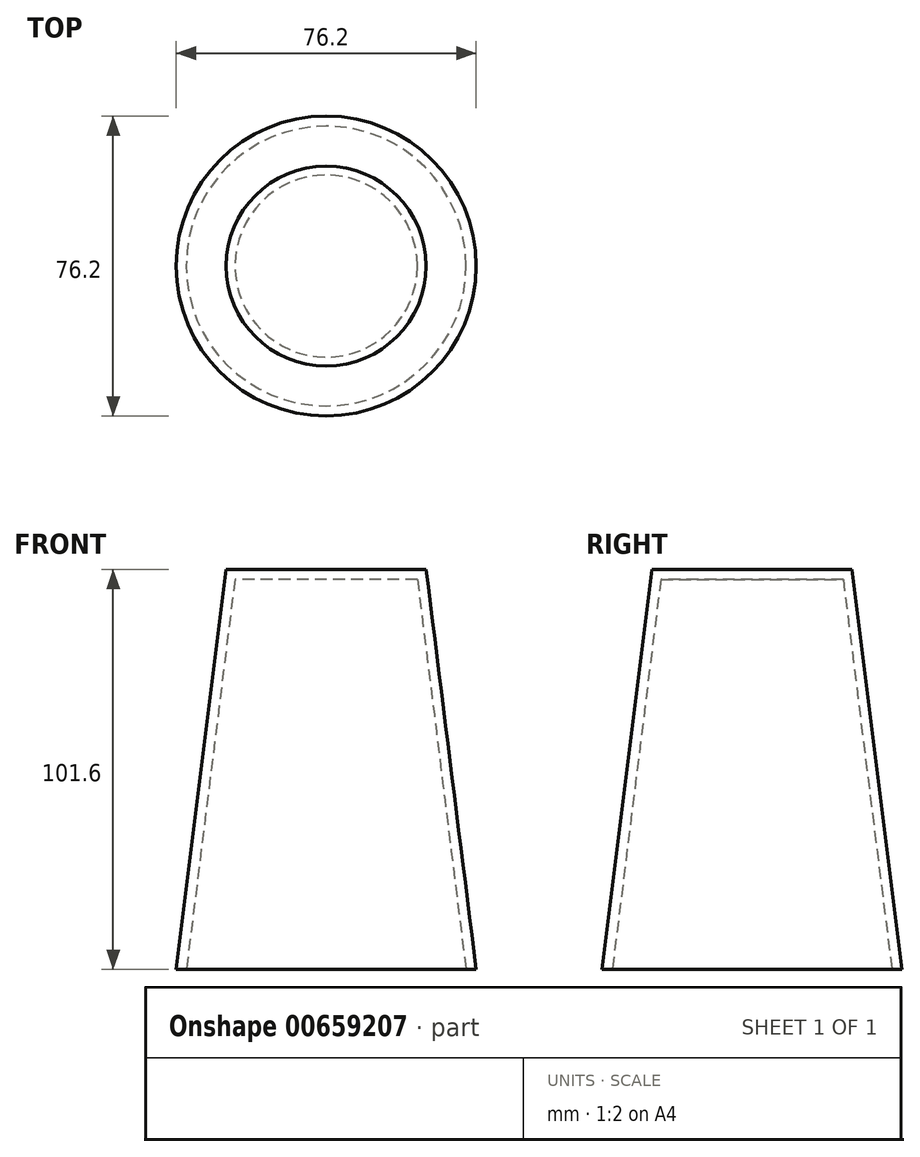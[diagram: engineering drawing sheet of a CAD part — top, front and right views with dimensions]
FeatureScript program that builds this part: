
annotation { "Feature Type Name" : "Feature", "Feature Type Description" : "" }
export const myFeature = defineFeature(function(context is Context, id is Id, definition is map)
    precondition{}
    {
        {
            var Q0;
            Q0=qCreatedBy(makeId("Top.planeOp"),FACE);
            var sketch = newSketch(context, id + "F0", { "sketchPlane" : qUnion([Q0])});
            skCircle(sketch, "E0", {"center": v(0, 0) * mm, "radius": 38.1 * mm});
            skSolve(sketch);
        }
        {
            var Q0;
            Q0=makeQuery(id+"F0.imprint","IMPRINT",FACE,{"disambiguationData":[TD([[makeQuery(id+"F0.imprint","IMPRINT",EDGE,{"derivedFrom":sQuery(id+"F0.wireOp",EDGE,"E0")}),1.0]])]});
            cPlane(context, id + "F1", {"entities" : qUnion([Q0]), "cplaneType" : CPlaneType.OFFSET, "offset" : 101.6 * mm, "width" : 152.4 * mm, "height" : 152.4 * mm});
        }
        {
            var Q0;
            Q0=qCreatedBy(id+"F1.planeOp",FACE);
            var sketch = newSketch(context, id + "F2", { "sketchPlane" : qUnion([Q0])});
            skCircle(sketch, "E1", {"center": v(0, 0) * mm, "radius": 25.4 * mm});
            skSolve(sketch);
        }
        {
            var Q0;
            Q0=makeQuery(id+"F0.imprint","IMPRINT",FACE,{"disambiguationData":[TD([[makeQuery(id+"F0.imprint","IMPRINT",EDGE,{"derivedFrom":sQuery(id+"F0.wireOp",EDGE,"E0")}),1.0]])]});
            var Q1;
            Q1=makeQuery(id+"F2.imprint","IMPRINT",FACE,{"disambiguationData":[TD([[makeQuery(id+"F2.imprint","IMPRINT",EDGE,{"derivedFrom":sQuery(id+"F2.wireOp",EDGE,"E1")}),1.0]])]});
            loft(context, id + "F3", {"sheetProfilesArray" : [{ "sheetProfileEntities" : qUnion([Q0]) }, { "sheetProfileEntities" : qUnion([Q1]) }]});
        }
        {
            var Q0;
            Q0=makeQuery(id+"F3.opLoft","CAP_FACE",FACE,{"disambiguationData":[OSD([makeQuery(id+"F0.imprint","IMPRINT",FACE,{"disambiguationData":[TD([[makeQuery(id+"F0.imprint","IMPRINT",EDGE,{"derivedFrom":sQuery(id+"F0.wireOp",EDGE,"E0")}),1.0]])]})])],"isStart":true});
            shell(context, id + "F4", {"entities" : qUnion([Q0]), "thickness" : 2.54 * mm});
        }
    });
